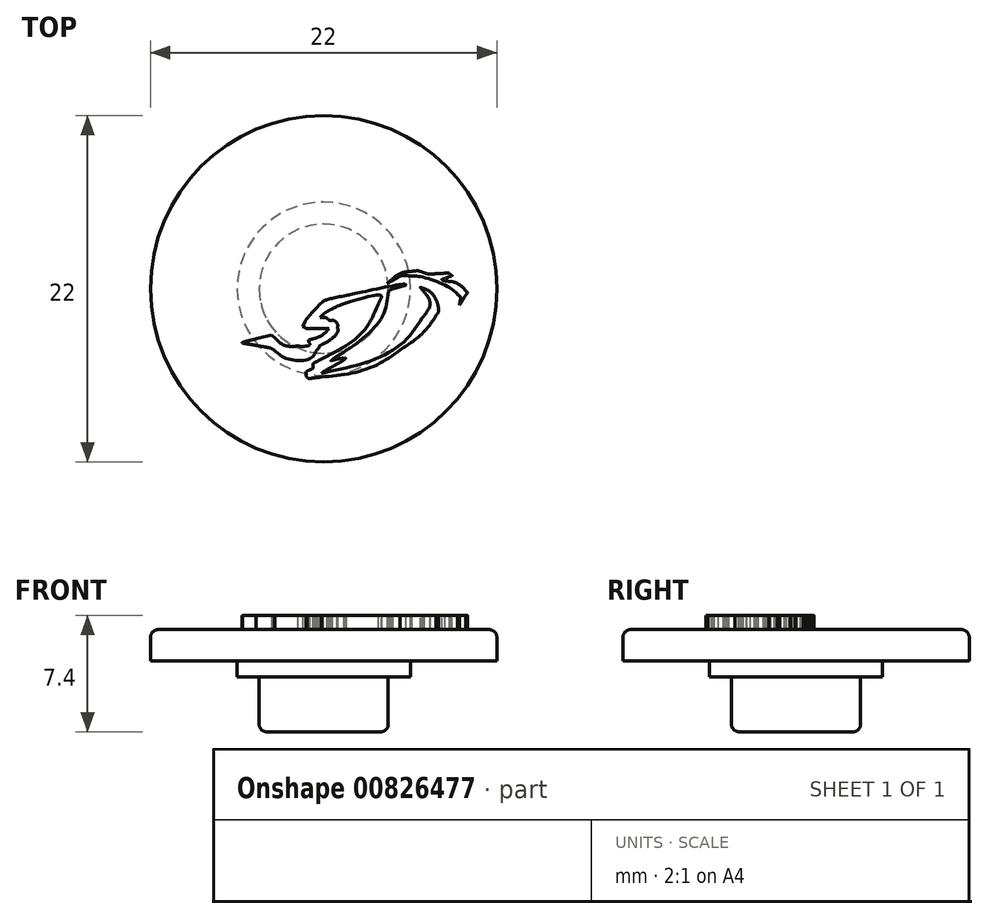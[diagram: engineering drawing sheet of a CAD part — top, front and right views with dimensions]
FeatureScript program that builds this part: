
annotation { "Feature Type Name" : "Feature", "Feature Type Description" : "" }
export const myFeature = defineFeature(function(context is Context, id is Id, definition is map)
    precondition{}
    {
        {
            var Q0;
            Q0=qCreatedBy(makeId("Top.planeOp"),FACE);
            var sketch = newSketch(context, id + "F0", { "sketchPlane" : qUnion([Q0])});
            skFitSpline(sketch, "E0", {"points": [v(-1.06, -5.63) * mm, v(-1.1, -5.6) * mm, v(-1.12, -5.5) * mm, v(-1.12, -5.4) * mm]});
            skFitSpline(sketch, "E1", {"points": [v(-1.12, -5.4) * mm, v(-1.12, -5.29) * mm, v(-1.08, -5.24) * mm, v(-0.9, -5.16) * mm]});
            skFitSpline(sketch, "E2", {"points": [v(-0.9, -5.16) * mm, v(-0.71, -5.08) * mm, v(-0.68, -5.03) * mm, v(-0.68, -4.9) * mm]});
            skFitSpline(sketch, "E3", {"points": [v(-0.68, -4.9) * mm, v(-0.68, -4.78) * mm, v(-0.63, -4.72) * mm, v(-0.5, -4.65) * mm]});
            skFitSpline(sketch, "E4", {"points": [v(-0.5, -4.65) * mm, v(1.5, -3.55) * mm, v(2.75, -2.4) * mm, v(3.43, -1.03) * mm]});
            skFitSpline(sketch, "E5", {"points": [v(3.43, -1.03) * mm, v(3.58, -0.74) * mm, v(3.68, -0.5) * mm, v(3.66, -0.48) * mm]});
            skFitSpline(sketch, "E6", {"points": [v(3.66, -0.48) * mm, v(3.57, -0.4) * mm, v(1.07, -1.04) * mm, v(0.53, -1.29) * mm]});
            skFitSpline(sketch, "E7", {"points": [v(0.53, -1.29) * mm, v(0.34, -1.37) * mm, v(0.09, -1.53) * mm, v(-0.03, -1.64) * mm]});
            skFitSpline(sketch, "E8", {"points": [v(-0.05, -1.83) * mm, v(0.06, -1.83) * mm, v(0.2, -1.87) * mm, v(0.26, -1.92) * mm]});
            skFitSpline(sketch, "E9", {"points": [v(0.26, -1.92) * mm, v(0.32, -1.97) * mm, v(0.42, -2.02) * mm, v(0.49, -2.02) * mm]});
            skFitSpline(sketch, "E10", {"points": [v(0.49, -2.02) * mm, v(0.66, -2.02) * mm, v(0.88, -2.26) * mm, v(0.88, -2.45) * mm]});
            skFitSpline(sketch, "E11", {"points": [v(0.88, -2.45) * mm, v(0.88, -2.74) * mm, v(0.48, -3.2) * mm, v(-0.04, -3.5) * mm]});
            skFitSpline(sketch, "E12", {"points": [v(-0.04, -3.5) * mm, v(-0.18, -3.58) * mm, v(-0.29, -3.66) * mm, v(-0.29, -3.7) * mm]});
            skFitSpline(sketch, "E13", {"points": [v(-0.29, -3.7) * mm, v(-0.29, -3.72) * mm, v(-0.36, -3.83) * mm, v(-0.46, -3.93) * mm]});
            skFitSpline(sketch, "E14", {"points": [v(-0.46, -3.93) * mm, v(-0.91, -4.45) * mm, v(-2.3, -4.45) * mm, v(-3.14, -3.92) * mm]});
            skFitSpline(sketch, "E15", {"points": [v(-3.14, -3.92) * mm, v(-3.35, -3.79) * mm, v(-3.55, -3.73) * mm, v(-4.3, -3.6) * mm]});
            skFitSpline(sketch, "E16", {"points": [v(-4.3, -3.6) * mm, v(-4.79, -3.52) * mm, v(-5.18, -3.44) * mm, v(-5.17, -3.42) * mm]});
            skFitSpline(sketch, "E17", {"points": [v(-5.17, -3.42) * mm, v(-5.16, -3.41) * mm, v(-4.74, -3.3) * mm, v(-4.23, -3.16) * mm]});
            skLineSegment(sketch, "E18", {"start": v(-0.03, -1.64) * mm, "end": v(-0.25, -1.83) * mm});
            skLineSegment(sketch, "E19", {"start": v(-0.25, -1.83) * mm, "end": v(-0.05, -1.83) * mm});
            skFitSpline(sketch, "E20", {"points": [v(-3.06, -3.16) * mm, v(-2.68, -3.5) * mm, v(-2.27, -3.65) * mm, v(-1.67, -3.65) * mm]});
            skFitSpline(sketch, "E21", {"points": [v(-1.67, -3.65) * mm, v(-1.13, -3.65) * mm, v(-0.89, -3.55) * mm, v(-0.94, -3.37) * mm]});
            skFitSpline(sketch, "E22", {"points": [v(-0.94, -3.37) * mm, v(-0.96, -3.28) * mm, v(-0.91, -3.25) * mm, v(-0.72, -3.2) * mm]});
            skFitSpline(sketch, "E23", {"points": [v(-0.72, -3.2) * mm, v(-0.4, -3.1) * mm, v(0.01, -2.87) * mm, v(0.19, -2.68) * mm]});
            skLineSegment(sketch, "E24", {"start": v(-4.23, -3.16) * mm, "end": v(-3.32, -2.92) * mm});
            skLineSegment(sketch, "E25", {"start": v(-3.32, -2.92) * mm, "end": v(-3.06, -3.16) * mm});
            skFitSpline(sketch, "E26", {"points": [v(-0.35, -2.53) * mm, v(-0.78, -2.54) * mm, v(-1.1, -2.52) * mm, v(-1.2, -2.47) * mm]});
            skLineSegment(sketch, "E27", {"start": v(0.19, -2.68) * mm, "end": v(0.34, -2.53) * mm});
            skLineSegment(sketch, "E28", {"start": v(0.34, -2.53) * mm, "end": v(-0.35, -2.53) * mm});
            skFitSpline(sketch, "E29", {"points": [v(-1.2, -2.11) * mm, v(-1.1, -1.95) * mm, v(-0.85, -1.63) * mm, v(-0.62, -1.4) * mm]});
            skFitSpline(sketch, "E30", {"points": [v(-0.62, -1.4) * mm, v(-0.06, -0.83) * mm, v(0.27, -0.67) * mm, v(1.42, -0.43) * mm]});
            skFitSpline(sketch, "E31", {"points": [v(1.42, -0.43) * mm, v(2.5, -0.2) * mm, v(5.18, 0.29) * mm, v(5.21, 0.25) * mm]});
            skFitSpline(sketch, "E32", {"points": [v(5.21, 0.25) * mm, v(5.22, 0.24) * mm, v(5.03, 0.17) * mm, v(4.77, 0.1) * mm]});
            skFitSpline(sketch, "E33", {"points": [v(4.77, 0.1) * mm, v(4.52, 0.03) * mm, v(4.27, -0.05) * mm, v(4.23, -0.07) * mm]});
            skFitSpline(sketch, "E34", {"points": [v(4.23, -0.07) * mm, v(4.18, -0.1) * mm, v(4.1, -0.25) * mm, v(4.07, -0.4) * mm]});
            skFitSpline(sketch, "E35", {"points": [v(4.07, -0.4) * mm, v(3.8, -1.62) * mm, v(2.55, -3.1) * mm, v(0.83, -4.3) * mm]});
            skFitSpline(sketch, "E36", {"points": [v(0.83, -4.3) * mm, v(0.6, -4.46) * mm, v(0.46, -4.58) * mm, v(0.52, -4.56) * mm]});
            skFitSpline(sketch, "E37", {"points": [v(0.52, -4.56) * mm, v(0.8, -4.48) * mm, v(1.15, -4.42) * mm, v(1.27, -4.42) * mm]});
            skFitSpline(sketch, "E38", {"points": [v(1.27, -4.42) * mm, v(1.41, -4.42) * mm, v(1.41, -4.42) * mm, v(1.3, -4.5) * mm]});
            skFitSpline(sketch, "E39", {"points": [v(1.3, -4.5) * mm, v(1.24, -4.55) * mm, v(0.9, -4.75) * mm, v(0.54, -4.96) * mm]});
            skFitSpline(sketch, "E40", {"points": [v(0.54, -4.96) * mm, v(0.18, -5.16) * mm, v(-0.1, -5.33) * mm, v(-0.1, -5.34) * mm]});
            skFitSpline(sketch, "E41", {"points": [v(-0.1, -5.34) * mm, v(-0.09, -5.35) * mm, v(0.17, -5.3) * mm, v(0.47, -5.22) * mm]});
            skFitSpline(sketch, "E42", {"points": [v(0.47, -5.22) * mm, v(3.05, -4.56) * mm, v(5.1, -3.36) * mm, v(6.26, -1.86) * mm]});
            skFitSpline(sketch, "E43", {"points": [v(6.26, -1.86) * mm, v(6.51, -1.53) * mm, v(6.74, -1.12) * mm, v(6.74, -1) * mm]});
            skFitSpline(sketch, "E44", {"points": [v(6.74, -1) * mm, v(6.74, -0.79) * mm, v(6.6, -0.47) * mm, v(6.37, -0.2) * mm]});
            skFitSpline(sketch, "E45", {"points": [v(6.37, -0.2) * mm, v(6.14, 0.08) * mm, v(6.14, 0.1) * mm, v(6.28, 0.04) * mm]});
            skFitSpline(sketch, "E46", {"points": [v(6.28, 0.04) * mm, v(6.55, -0.06) * mm, v(6.95, -0.39) * mm, v(7.1, -0.64) * mm]});
            skFitSpline(sketch, "E47", {"points": [v(7.1, -0.64) * mm, v(7.18, -0.78) * mm, v(7.26, -1.01) * mm, v(7.28, -1.17) * mm]});
            skFitSpline(sketch, "E48", {"points": [v(7.28, -1.17) * mm, v(7.3, -1.42) * mm, v(7.3, -1.47) * mm, v(7.13, -1.7) * mm]});
            skFitSpline(sketch, "E49", {"points": [v(7.13, -1.7) * mm, v(6.62, -2.45) * mm, v(5.76, -3.27) * mm, v(4.84, -3.88) * mm]});
            skFitSpline(sketch, "E50", {"points": [v(4.84, -3.88) * mm, v(3.56, -4.74) * mm, v(1.78, -5.36) * mm, v(-0.14, -5.6) * mm]});
            skFitSpline(sketch, "E51", {"points": [v(-0.14, -5.6) * mm, v(-0.95, -5.71) * mm, v(-0.97, -5.71) * mm, v(-1.06, -5.63) * mm]});
            skLineSegment(sketch, "E52", {"start": v(-1.2, -2.47) * mm, "end": v(-1.35, -2.4) * mm});
            skLineSegment(sketch, "E53", {"start": v(-1.35, -2.4) * mm, "end": v(-1.2, -2.11) * mm});
            skFitSpline(sketch, "E54", {"points": [v(-5.56, -2.37) * mm, v(-5.18, -1.6) * mm, v(-5.14, -0.8) * mm, v(-5.47, -0.19) * mm]});
            skFitSpline(sketch, "E55", {"points": [v(-5.47, -0.19) * mm, v(-6.03, 0.87) * mm, v(-7.3, 1.6) * mm, v(-9.85, 2.35) * mm]});
            skFitSpline(sketch, "E56", {"points": [v(-9.85, 2.35) * mm, v(-10.11, 2.43) * mm, v(-10.08, 2.43) * mm, v(-8.98, 2.44) * mm]});
            skFitSpline(sketch, "E57", {"points": [v(-8.98, 2.44) * mm, v(-8.05, 2.44) * mm, v(-7.74, 2.46) * mm, v(-7.29, 2.55) * mm]});
            skFitSpline(sketch, "E58", {"points": [v(-7.29, 2.55) * mm, v(-6.56, 2.7) * mm, v(-6.58, 2.7) * mm, v(-6.7, 2.46) * mm]});
            skFitSpline(sketch, "E59", {"points": [v(-6.7, 2.46) * mm, v(-6.9, 2.05) * mm, v(-6.9, 2.03) * mm, v(-6.56, 1.87) * mm]});
            skLineSegment(sketch, "E60", {"start": v(-1.06, -5.63) * mm, "end": v(-1.06, -5.63) * mm});
            skFitSpline(sketch, "E61", {"points": [v(-6.01, 2.05) * mm, v(-5.8, 2.33) * mm, v(-5.16, 2.83) * mm, v(-5.02, 2.83) * mm]});
            skFitSpline(sketch, "E62", {"points": [v(-5.02, 2.83) * mm, v(-4.93, 2.83) * mm, v(-4.97, 2.71) * mm, v(-5.14, 2.5) * mm]});
            skFitSpline(sketch, "E63", {"points": [v(-5.14, 2.5) * mm, v(-5.3, 2.3) * mm, v(-5.6, 1.7) * mm, v(-5.66, 1.47) * mm]});
            skFitSpline(sketch, "E64", {"points": [v(-5.66, 1.47) * mm, v(-5.68, 1.38) * mm, v(-5.62, 1.3) * mm, v(-5.4, 1.13) * mm]});
            skLineSegment(sketch, "E65", {"start": v(-6.56, 1.87) * mm, "end": v(-6.26, 1.73) * mm});
            skLineSegment(sketch, "E66", {"start": v(-6.26, 1.73) * mm, "end": v(-6.01, 2.05) * mm});
            skFitSpline(sketch, "E67", {"points": [v(-4.98, 1.2) * mm, v(-4.9, 1.36) * mm, v(-4.76, 1.6) * mm, v(-4.65, 1.75) * mm]});
            skFitSpline(sketch, "E68", {"points": [v(-4.65, 1.75) * mm, v(-4.46, 2) * mm, v(-3.84, 2.5) * mm, v(-3.74, 2.5) * mm]});
            skFitSpline(sketch, "E69", {"points": [v(-3.74, 2.5) * mm, v(-3.63, 2.5) * mm, v(-3.7, 2.32) * mm, v(-3.93, 1.98) * mm]});
            skFitSpline(sketch, "E70", {"points": [v(-3.93, 1.98) * mm, v(-4.28, 1.47) * mm, v(-4.4, 1) * mm, v(-4.47, 0.07) * mm]});
            skFitSpline(sketch, "E71", {"points": [v(-4.47, 0.07) * mm, v(-4.52, -0.75) * mm, v(-4.61, -1.2) * mm, v(-4.8, -1.59) * mm]});
            skFitSpline(sketch, "E72", {"points": [v(-4.8, -1.59) * mm, v(-4.98, -1.92) * mm, v(-5.33, -2.38) * mm, v(-5.53, -2.52) * mm]});
            skLineSegment(sketch, "E73", {"start": v(-5.4, 1.13) * mm, "end": v(-5.1, 0.9) * mm});
            skLineSegment(sketch, "E74", {"start": v(-5.1, 0.9) * mm, "end": v(-4.98, 1.2) * mm});
            skFitSpline(sketch, "E75", {"points": [v(-3.23, -2.03) * mm, v(-3.24, -1.56) * mm, v(-3.08, -1.14) * mm, v(-2.74, -0.77) * mm]});
            skFitSpline(sketch, "E76", {"points": [v(-2.74, -0.77) * mm, v(-2.59, -0.6) * mm, v(-2.35, -0.41) * mm, v(-2.21, -0.34) * mm]});
            skFitSpline(sketch, "E77", {"points": [v(-2.21, -0.34) * mm, v(-2, -0.22) * mm, v(-1.94, -0.17) * mm, v(-1.87, 0.07) * mm]});
            skFitSpline(sketch, "E78", {"points": [v(-1.87, 0.07) * mm, v(-1.78, 0.38) * mm, v(-1.77, 0.65) * mm, v(-1.84, 0.77) * mm]});
            skFitSpline(sketch, "E79", {"points": [v(-1.84, 0.77) * mm, v(-1.92, 0.88) * mm, v(-2.24, 0.82) * mm, v(-2.8, 0.58) * mm]});
            skFitSpline(sketch, "E80", {"points": [v(-2.8, 0.58) * mm, v(-3.7, 0.2) * mm, v(-3.91, -0.03) * mm, v(-3.9, -0.59) * mm]});
            skFitSpline(sketch, "E81", {"points": [v(-3.9, -0.59) * mm, v(-3.9, -0.78) * mm, v(-3.89, -1.02) * mm, v(-3.86, -1.14) * mm]});
            skFitSpline(sketch, "E82", {"points": [v(-3.86, -1.14) * mm, v(-3.83, -1.25) * mm, v(-3.83, -1.33) * mm, v(-3.85, -1.32) * mm]});
            skFitSpline(sketch, "E83", {"points": [v(-3.85, -1.32) * mm, v(-3.95, -1.26) * mm, v(-4.03, -0.54) * mm, v(-4, -0.07) * mm]});
            skFitSpline(sketch, "E84", {"points": [v(-4, -0.07) * mm, v(-3.97, 0.46) * mm, v(-3.83, 0.92) * mm, v(-3.55, 1.34) * mm]});
            skLineSegment(sketch, "E85", {"start": v(-5.53, -2.52) * mm, "end": v(-5.7, -2.64) * mm});
            skLineSegment(sketch, "E86", {"start": v(-5.7, -2.64) * mm, "end": v(-5.56, -2.37) * mm});
            skFitSpline(sketch, "E87", {"points": [v(-1.57, 1.6) * mm, v(0.18, 1.6) * mm, v(0.24, 1.61) * mm, v(0.43, 1.73) * mm]});
            skFitSpline(sketch, "E88", {"points": [v(0.43, 1.73) * mm, v(1.18, 2.18) * mm, v(1.72, 2.78) * mm, v(1.83, 3.3) * mm]});
            skFitSpline(sketch, "E89", {"points": [v(1.83, 3.3) * mm, v(1.9, 3.58) * mm, v(1.85, 3.94) * mm, v(1.7, 4.29) * mm]});
            skFitSpline(sketch, "E90", {"points": [v(1.7, 4.29) * mm, v(1.66, 4.37) * mm, v(1.74, 4.38) * mm, v(2.23, 4.42) * mm]});
            skFitSpline(sketch, "E91", {"points": [v(2.23, 4.42) * mm, v(2.55, 4.44) * mm, v(2.93, 4.47) * mm, v(3.09, 4.48) * mm]});
            skLineSegment(sketch, "E92", {"start": v(-3.55, 1.34) * mm, "end": v(-3.38, 1.6) * mm});
            skLineSegment(sketch, "E93", {"start": v(-3.38, 1.6) * mm, "end": v(-1.57, 1.6) * mm});
            skFitSpline(sketch, "E94", {"points": [v(3.2, 4.42) * mm, v(2.95, 4.28) * mm, v(2.62, 3.95) * mm, v(2.48, 3.7) * mm]});
            skFitSpline(sketch, "E95", {"points": [v(2.48, 3.7) * mm, v(2.38, 3.52) * mm, v(2.36, 3.38) * mm, v(2.36, 2.97) * mm]});
            skFitSpline(sketch, "E96", {"points": [v(2.36, 2.97) * mm, v(2.36, 2.45) * mm, v(2.41, 2.3) * mm, v(2.7, 1.9) * mm]});
            skLineSegment(sketch, "E97", {"start": v(3.09, 4.48) * mm, "end": v(3.36, 4.51) * mm});
            skLineSegment(sketch, "E98", {"start": v(3.36, 4.51) * mm, "end": v(3.2, 4.42) * mm});
            skFitSpline(sketch, "E99", {"points": [v(6.72, 1.57) * mm, v(7.03, 1.42) * mm, v(7.45, 1.37) * mm, v(7.76, 1.46) * mm]});
            skLineSegment(sketch, "E100", {"start": v(2.7, 1.9) * mm, "end": v(2.84, 1.72) * mm});
            skLineSegment(sketch, "E101", {"start": v(2.84, 1.72) * mm, "end": v(4.63, 1.72) * mm});
            skLineSegment(sketch, "E102", {"start": v(4.63, 1.72) * mm, "end": v(6.42, 1.72) * mm});
            skLineSegment(sketch, "E103", {"start": v(6.42, 1.72) * mm, "end": v(6.72, 1.57) * mm});
            skFitSpline(sketch, "E104", {"points": [v(7.53, 1.91) * mm, v(7.15, 2.31) * mm, v(6.96, 2.62) * mm, v(6.96, 2.8) * mm]});
            skFitSpline(sketch, "E105", {"points": [v(6.96, 2.8) * mm, v(6.96, 2.97) * mm, v(6.67, 3.54) * mm, v(6.44, 3.8) * mm]});
            skLineSegment(sketch, "E106", {"start": v(7.76, 1.46) * mm, "end": v(7.92, 1.5) * mm});
            skLineSegment(sketch, "E107", {"start": v(7.92, 1.5) * mm, "end": v(7.53, 1.91) * mm});
            skFitSpline(sketch, "E108", {"points": [v(6.54, 3.9) * mm, v(7.28, 3.49) * mm, v(7.31, 3.45) * mm, v(7.4, 3.06) * mm]});
            skFitSpline(sketch, "E109", {"points": [v(7.4, 3.06) * mm, v(7.47, 2.66) * mm, v(7.5, 2.6) * mm, v(7.85, 2.21) * mm]});
            skFitSpline(sketch, "E110", {"points": [v(7.85, 2.21) * mm, v(8.02, 2.02) * mm, v(8.24, 1.86) * mm, v(8.73, 1.62) * mm]});
            skLineSegment(sketch, "E111", {"start": v(6.44, 3.8) * mm, "end": v(6.2, 4.09) * mm});
            skLineSegment(sketch, "E112", {"start": v(6.2, 4.09) * mm, "end": v(6.54, 3.9) * mm});
            skFitSpline(sketch, "E113", {"points": [v(9.7, -0.6) * mm, v(9.54, -0.8) * mm, v(9.36, -1.06) * mm, v(9.3, -1.18) * mm]});
            skFitSpline(sketch, "E114", {"points": [v(9.3, -1.18) * mm, v(9.17, -1.44) * mm, v(9.13, -1.47) * mm, v(8.63, -1.65) * mm]});
            skLineSegment(sketch, "E115", {"start": v(8.73, 1.62) * mm, "end": v(9.38, 1.28) * mm});
            skLineSegment(sketch, "E116", {"start": v(9.38, 1.28) * mm, "end": v(9.69, 0.53) * mm});
            skLineSegment(sketch, "E117", {"start": v(9.69, 0.53) * mm, "end": v(9.99, -0.22) * mm});
            skLineSegment(sketch, "E118", {"start": v(9.99, -0.22) * mm, "end": v(9.7, -0.6) * mm});
            skFitSpline(sketch, "E119", {"points": [v(8.61, -1.4) * mm, v(8.85, -1.14) * mm, v(9.09, -0.83) * mm, v(9.2, -0.6) * mm]});
            skLineSegment(sketch, "E120", {"start": v(8.63, -1.65) * mm, "end": v(8.21, -1.8) * mm});
            skLineSegment(sketch, "E121", {"start": v(8.21, -1.8) * mm, "end": v(8.61, -1.4) * mm});
            skFitSpline(sketch, "E122", {"points": [v(9.19, 0.08) * mm, v(9.07, 0.24) * mm, v(8.88, 0.45) * mm, v(8.77, 0.53) * mm]});
            skFitSpline(sketch, "E123", {"points": [v(8.77, 0.53) * mm, v(8.55, 0.71) * mm, v(8.53, 0.77) * mm, v(8.7, 0.77) * mm]});
            skFitSpline(sketch, "E124", {"points": [v(8.7, 0.77) * mm, v(8.84, 0.77) * mm, v(9.02, 0.87) * mm, v(9.02, 0.94) * mm]});
            skFitSpline(sketch, "E125", {"points": [v(9.02, 0.94) * mm, v(9.02, 0.98) * mm, v(8.81, 1.1) * mm, v(8.55, 1.22) * mm]});
            skLineSegment(sketch, "E126", {"start": v(9.2, -0.6) * mm, "end": v(9.41, -0.21) * mm});
            skLineSegment(sketch, "E127", {"start": v(9.41, -0.21) * mm, "end": v(9.19, 0.08) * mm});
            skFitSpline(sketch, "E128", {"points": [v(7.82, 1.32) * mm, v(7.45, 1.16) * mm, v(6.85, 1.12) * mm, v(6.4, 1.25) * mm]});
            skFitSpline(sketch, "E129", {"points": [v(6.4, 1.25) * mm, v(5.72, 1.43) * mm, v(4.97, 1.3) * mm, v(4.35, 0.9) * mm]});
            skLineSegment(sketch, "E130", {"start": v(8.55, 1.22) * mm, "end": v(8.08, 1.44) * mm});
            skLineSegment(sketch, "E131", {"start": v(8.08, 1.44) * mm, "end": v(7.82, 1.32) * mm});
            skFitSpline(sketch, "E132", {"points": [v(4.06, 0.91) * mm, v(4.06, 1.17) * mm, v(3.94, 1.21) * mm, v(3.3, 1.22) * mm]});
            skFitSpline(sketch, "E133", {"points": [v(3.3, 1.22) * mm, v(2.7, 1.23) * mm, v(2.58, 1.18) * mm, v(2.2, 0.82) * mm]});
            skLineSegment(sketch, "E134", {"start": v(4.35, 0.9) * mm, "end": v(4.06, 0.71) * mm});
            skLineSegment(sketch, "E135", {"start": v(4.06, 0.71) * mm, "end": v(4.06, 0.91) * mm});
            skFitSpline(sketch, "E136", {"points": [v(1.64, 0.6) * mm, v(1.4, 0.67) * mm, v(1.39, 0.68) * mm, v(1.39, 0.88) * mm]});
            skFitSpline(sketch, "E137", {"points": [v(1.39, 0.88) * mm, v(1.39, 0.99) * mm, v(1.41, 1.17) * mm, v(1.44, 1.27) * mm]});
            skLineSegment(sketch, "E138", {"start": v(2.2, 0.82) * mm, "end": v(1.9, 0.54) * mm});
            skLineSegment(sketch, "E139", {"start": v(1.9, 0.54) * mm, "end": v(1.64, 0.6) * mm});
            skFitSpline(sketch, "E140", {"points": [v(1.36, 1.31) * mm, v(1.28, 1.23) * mm, v(1.18, 1.04) * mm, v(1.13, 0.89) * mm]});
            skFitSpline(sketch, "E141", {"points": [v(1.13, 0.89) * mm, v(1.04, 0.64) * mm, v(1.01, 0.61) * mm, v(0.83, 0.59) * mm]});
            skFitSpline(sketch, "E142", {"points": [v(0.83, 0.59) * mm, v(0.72, 0.58) * mm, v(0.62, 0.58) * mm, v(0.6, 0.59) * mm]});
            skFitSpline(sketch, "E143", {"points": [v(0.6, 0.59) * mm, v(0.6, 0.6) * mm, v(0.56, 0.75) * mm, v(0.55, 0.93) * mm]});
            skLineSegment(sketch, "E144", {"start": v(1.44, 1.27) * mm, "end": v(1.5, 1.47) * mm});
            skLineSegment(sketch, "E145", {"start": v(1.5, 1.47) * mm, "end": v(1.36, 1.31) * mm});
            skFitSpline(sketch, "E146", {"points": [v(0.42, 1.03) * mm, v(0.37, 0.91) * mm, v(0.33, 0.74) * mm, v(0.33, 0.66) * mm]});
            skFitSpline(sketch, "E147", {"points": [v(0.33, 0.66) * mm, v(0.33, 0.56) * mm, v(0.28, 0.47) * mm, v(0.18, 0.41) * mm]});
            skFitSpline(sketch, "E148", {"points": [v(0.18, 0.41) * mm, v(0.01, 0.3) * mm, v(0.02, 0.3) * mm, v(-0.15, 0.64) * mm]});
            skLineSegment(sketch, "E149", {"start": v(0.55, 0.93) * mm, "end": v(0.52, 1.24) * mm});
            skLineSegment(sketch, "E150", {"start": v(0.52, 1.24) * mm, "end": v(0.42, 1.03) * mm});
            skFitSpline(sketch, "E151", {"points": [v(-0.28, 0.55) * mm, v(-0.26, 0.19) * mm, v(-0.35, -0.07) * mm, v(-0.49, -0.07) * mm]});
            skFitSpline(sketch, "E152", {"points": [v(-0.49, -0.07) * mm, v(-0.52, -0.07) * mm, v(-0.64, 0.02) * mm, v(-0.75, 0.13) * mm]});
            skLineSegment(sketch, "E153", {"start": v(-0.15, 0.64) * mm, "end": v(-0.29, 0.91) * mm});
            skLineSegment(sketch, "E154", {"start": v(-0.29, 0.91) * mm, "end": v(-0.28, 0.55) * mm});
            skFitSpline(sketch, "E155", {"points": [v(-0.92, 0.18) * mm, v(-0.9, 0.09) * mm, v(-0.85, -0.05) * mm, v(-0.81, -0.14) * mm]});
            skFitSpline(sketch, "E156", {"points": [v(-0.81, -0.14) * mm, v(-0.77, -0.23) * mm, v(-0.75, -0.36) * mm, v(-0.77, -0.43) * mm]});
            skFitSpline(sketch, "E157", {"points": [v(-0.77, -0.43) * mm, v(-0.8, -0.54) * mm, v(-0.83, -0.56) * mm, v(-1.3, -0.58) * mm]});
            skFitSpline(sketch, "E158", {"points": [v(-1.3, -0.58) * mm, v(-1.72, -0.6) * mm, v(-1.87, -0.63) * mm, v(-2.1, -0.75) * mm]});
            skFitSpline(sketch, "E159", {"points": [v(-2.1, -0.75) * mm, v(-2.62, -1.02) * mm, v(-3.08, -1.6) * mm, v(-3.18, -2.15) * mm]});
            skFitSpline(sketch, "E160", {"points": [v(-3.18, -2.15) * mm, v(-3.23, -2.37) * mm, v(-3.23, -2.37) * mm, v(-3.23, -2.03) * mm]});
            skLineSegment(sketch, "E161", {"start": v(-0.75, 0.13) * mm, "end": v(-0.96, 0.33) * mm});
            skLineSegment(sketch, "E162", {"start": v(-0.96, 0.33) * mm, "end": v(-0.92, 0.18) * mm});
            skFitSpline(sketch, "E163", {"points": [v(8.67, -0.79) * mm, v(8.7, -0.54) * mm, v(8.7, -0.52) * mm, v(8.49, -0.35) * mm]});
            skFitSpline(sketch, "E164", {"points": [v(8.49, -0.35) * mm, v(7.97, 0.08) * mm, v(6.23, 0.75) * mm, v(5.49, 0.81) * mm]});
            skFitSpline(sketch, "E165", {"points": [v(5.49, 0.81) * mm, v(5.02, 0.85) * mm, v(4.83, 0.8) * mm, v(4.36, 0.52) * mm]});
            skFitSpline(sketch, "E166", {"points": [v(4.26, 0.52) * mm, v(4.6, 0.83) * mm, v(5.1, 1.04) * mm, v(5.57, 1.1) * mm]});
            skFitSpline(sketch, "E167", {"points": [v(5.57, 1.1) * mm, v(5.93, 1.15) * mm, v(6.03, 1.14) * mm, v(6.32, 1.04) * mm]});
            skFitSpline(sketch, "E168", {"points": [v(6.32, 1.04) * mm, v(6.61, 0.94) * mm, v(6.73, 0.93) * mm, v(7.3, 0.96) * mm]});
            skFitSpline(sketch, "E169", {"points": [v(7.3, 0.96) * mm, v(7.82, 1) * mm, v(7.96, 0.99) * mm, v(8.05, 0.92) * mm]});
            skFitSpline(sketch, "E170", {"points": [v(8.05, 0.92) * mm, v(8.16, 0.84) * mm, v(8.15, 0.83) * mm, v(8, 0.77) * mm]});
            skFitSpline(sketch, "E171", {"points": [v(8, 0.77) * mm, v(7.9, 0.73) * mm, v(7.76, 0.68) * mm, v(7.68, 0.65) * mm]});
            skFitSpline(sketch, "E172", {"points": [v(7.68, 0.65) * mm, v(7.51, 0.58) * mm, v(7.6, 0.52) * mm, v(7.95, 0.47) * mm]});
            skFitSpline(sketch, "E173", {"points": [v(7.95, 0.47) * mm, v(8.28, 0.42) * mm, v(8.73, 0.19) * mm, v(8.96, -0.05) * mm]});
            skFitSpline(sketch, "E174", {"points": [v(8.96, -0.05) * mm, v(9.13, -0.23) * mm, v(9.13, -0.25) * mm, v(9.05, -0.36) * mm]});
            skFitSpline(sketch, "E175", {"points": [v(9.05, -0.36) * mm, v(9, -0.43) * mm, v(8.9, -0.6) * mm, v(8.8, -0.76) * mm]});
            skLineSegment(sketch, "E176", {"start": v(4.36, 0.52) * mm, "end": v(4.03, 0.32) * mm});
            skLineSegment(sketch, "E177", {"start": v(4.03, 0.32) * mm, "end": v(4.26, 0.52) * mm});
            skFitSpline(sketch, "E178", {"points": [v(-1.07, 2.14) * mm, v(-1.07, 2.15) * mm, v(-1.03, 2.26) * mm, v(-0.99, 2.36) * mm]});
            skLineSegment(sketch, "E179", {"start": v(8.8, -0.76) * mm, "end": v(8.63, -1.04) * mm});
            skLineSegment(sketch, "E180", {"start": v(8.63, -1.04) * mm, "end": v(8.67, -0.79) * mm});
            skFitSpline(sketch, "E181", {"points": [v(-1.18, 2.67) * mm, v(-1.42, 2.78) * mm, v(-1.84, 3.14) * mm, v(-1.78, 3.2) * mm]});
            skFitSpline(sketch, "E182", {"points": [v(-1.78, 3.2) * mm, v(-1.77, 3.2) * mm, v(-1.62, 3.15) * mm, v(-1.45, 3.07) * mm]});
            skFitSpline(sketch, "E183", {"points": [v(-1.45, 3.07) * mm, v(-1.25, 2.97) * mm, v(-1.03, 2.92) * mm, v(-0.76, 2.9) * mm]});
            skLineSegment(sketch, "E184", {"start": v(-0.99, 2.36) * mm, "end": v(-0.9, 2.55) * mm});
            skLineSegment(sketch, "E185", {"start": v(-0.9, 2.55) * mm, "end": v(-1.18, 2.67) * mm});
            skFitSpline(sketch, "E186", {"points": [v(0.01, 3.3) * mm, v(0.37, 3.7) * mm, v(0.4, 3.72) * mm, v(0.68, 3.76) * mm]});
            skFitSpline(sketch, "E187", {"points": [v(0.68, 3.76) * mm, v(1.18, 3.83) * mm, v(1.21, 3.86) * mm, v(0.9, 4) * mm]});
            skFitSpline(sketch, "E188", {"points": [v(0.9, 4) * mm, v(0.34, 4.23) * mm, v(0.34, 4.23) * mm, v(-0.06, 3.73) * mm]});
            skFitSpline(sketch, "E189", {"points": [v(-0.06, 3.73) * mm, v(-0.26, 3.48) * mm, v(-0.43, 3.29) * mm, v(-0.43, 3.3) * mm]});
            skFitSpline(sketch, "E190", {"points": [v(-0.43, 3.3) * mm, v(-0.44, 3.3) * mm, v(-0.38, 3.53) * mm, v(-0.29, 3.8) * mm]});
            skFitSpline(sketch, "E191", {"points": [v(-0.29, 3.8) * mm, v(-0.2, 4.07) * mm, v(-0.15, 4.3) * mm, v(-0.18, 4.31) * mm]});
            skFitSpline(sketch, "E192", {"points": [v(-0.18, 4.31) * mm, v(-0.22, 4.34) * mm, v(-0.84, 3.73) * mm, v(-0.9, 3.6) * mm]});
            skFitSpline(sketch, "E193", {"points": [v(-0.9, 3.6) * mm, v(-0.9, 3.58) * mm, v(-0.93, 3.56) * mm, v(-0.96, 3.56) * mm]});
            skFitSpline(sketch, "E194", {"points": [v(-0.96, 3.56) * mm, v(-0.98, 3.56) * mm, v(-0.93, 3.72) * mm, v(-0.84, 3.93) * mm]});
            skFitSpline(sketch, "E195", {"points": [v(-0.84, 3.93) * mm, v(-0.64, 4.37) * mm, v(-0.64, 4.4) * mm, v(-0.81, 4.4) * mm]});
            skFitSpline(sketch, "E196", {"points": [v(-0.81, 4.4) * mm, v(-0.9, 4.4) * mm, v(-1.02, 4.3) * mm, v(-1.18, 4.12) * mm]});
            skFitSpline(sketch, "E197", {"points": [v(-1.18, 4.12) * mm, v(-1.31, 3.96) * mm, v(-1.43, 3.85) * mm, v(-1.44, 3.86) * mm]});
            skFitSpline(sketch, "E198", {"points": [v(-1.44, 3.86) * mm, v(-1.45, 3.87) * mm, v(-1.44, 4) * mm, v(-1.41, 4.17) * mm]});
            skLineSegment(sketch, "E199", {"start": v(-0.76, 2.9) * mm, "end": v(-0.36, 2.88) * mm});
            skLineSegment(sketch, "E200", {"start": v(-0.36, 2.88) * mm, "end": v(0.01, 3.3) * mm});
            skFitSpline(sketch, "E201", {"points": [v(-1.83, 4.45) * mm, v(-2.24, 4.45) * mm, v(-2.3, 4.44) * mm, v(-2.24, 4.37) * mm]});
            skFitSpline(sketch, "E202", {"points": [v(-2.24, 4.37) * mm, v(-2.2, 4.31) * mm, v(-2.2, 4.23) * mm, v(-2.23, 4.07) * mm]});
            skFitSpline(sketch, "E203", {"points": [v(-2.23, 4.07) * mm, v(-2.29, 3.87) * mm, v(-2.31, 3.85) * mm, v(-2.51, 3.82) * mm]});
            skFitSpline(sketch, "E204", {"points": [v(-2.51, 3.82) * mm, v(-2.7, 3.79) * mm, v(-2.86, 3.83) * mm, v(-3.36, 4.01) * mm]});
            skFitSpline(sketch, "E205", {"points": [v(-3.36, 4.01) * mm, v(-4.04, 4.27) * mm, v(-4.04, 4.28) * mm, v(-3.45, 4.4) * mm]});
            skFitSpline(sketch, "E206", {"points": [v(-3.45, 4.4) * mm, v(-3.17, 4.45) * mm, v(-3.13, 4.47) * mm, v(-3.13, 4.59) * mm]});
            skFitSpline(sketch, "E207", {"points": [v(-3.13, 4.59) * mm, v(-3.13, 4.66) * mm, v(-3.1, 4.74) * mm, v(-3.05, 4.78) * mm]});
            skFitSpline(sketch, "E208", {"points": [v(-3.05, 4.78) * mm, v(-2.95, 4.87) * mm, v(-1.74, 4.96) * mm, v(-1.32, 4.92) * mm]});
            skFitSpline(sketch, "E209", {"points": [v(-1.32, 4.92) * mm, v(-1.03, 4.9) * mm, v(-0.66, 4.95) * mm, v(1.03, 5.29) * mm]});
            skLineSegment(sketch, "E210", {"start": v(-1.41, 4.17) * mm, "end": v(-1.36, 4.45) * mm});
            skLineSegment(sketch, "E211", {"start": v(-1.36, 4.45) * mm, "end": v(-1.83, 4.45) * mm});
            skFitSpline(sketch, "E212", {"points": [v(3.76, 5.37) * mm, v(4.16, 5.2) * mm, v(4.5, 5.04) * mm, v(4.52, 5.02) * mm]});
            skFitSpline(sketch, "E213", {"points": [v(4.52, 5.02) * mm, v(4.54, 5) * mm, v(4.2, 5) * mm, v(3.77, 5.02) * mm]});
            skFitSpline(sketch, "E214", {"points": [v(3.77, 5.02) * mm, v(3.06, 5.05) * mm, v(2.9, 5.04) * mm, v(2.36, 4.92) * mm]});
            skFitSpline(sketch, "E215", {"points": [v(2.36, 4.92) * mm, v(1.07, 4.65) * mm, v(0.38, 4.48) * mm, v(0.42, 4.45) * mm]});
            skFitSpline(sketch, "E216", {"points": [v(0.42, 4.45) * mm, v(0.45, 4.43) * mm, v(0.64, 4.35) * mm, v(0.86, 4.26) * mm]});
            skFitSpline(sketch, "E217", {"points": [v(0.86, 4.26) * mm, v(1.07, 4.18) * mm, v(1.3, 4.08) * mm, v(1.35, 4.03) * mm]});
            skFitSpline(sketch, "E218", {"points": [v(1.35, 4.03) * mm, v(1.5, 3.91) * mm, v(1.54, 3.43) * mm, v(1.4, 3.17) * mm]});
            skFitSpline(sketch, "E219", {"points": [v(1.4, 3.17) * mm, v(1.31, 3) * mm, v(1.27, 2.97) * mm, v(1, 2.93) * mm]});
            skFitSpline(sketch, "E220", {"points": [v(1, 2.93) * mm, v(0.58, 2.87) * mm, v(0.07, 2.62) * mm, v(-0.22, 2.34) * mm]});
            skFitSpline(sketch, "E221", {"points": [v(-0.22, 2.34) * mm, v(-0.44, 2.13) * mm, v(-0.48, 2.1) * mm, v(-0.76, 2.1) * mm]});
            skFitSpline(sketch, "E222", {"points": [v(-0.76, 2.1) * mm, v(-0.93, 2.1) * mm, v(-1.07, 2.12) * mm, v(-1.07, 2.14) * mm]});
            skLineSegment(sketch, "E223", {"start": v(1.03, 5.29) * mm, "end": v(3.04, 5.69) * mm});
            skLineSegment(sketch, "E224", {"start": v(3.04, 5.69) * mm, "end": v(3.76, 5.37) * mm});
            skFitSpline(sketch, "E225", {"points": [v(5.68, 2.27) * mm, v(5.68, 2.36) * mm, v(5.64, 2.37) * mm, v(5.41, 2.35) * mm]});
            skFitSpline(sketch, "E226", {"points": [v(5.41, 2.35) * mm, v(5.18, 2.32) * mm, v(5.12, 2.34) * mm, v(4.97, 2.47) * mm]});
            skFitSpline(sketch, "E227", {"points": [v(4.97, 2.47) * mm, v(4.86, 2.56) * mm, v(4.76, 2.7) * mm, v(4.73, 2.85) * mm]});
            skFitSpline(sketch, "E228", {"points": [v(4.73, 2.85) * mm, v(4.68, 3.03) * mm, v(4.55, 3.2) * mm, v(4.21, 3.55) * mm]});
            skFitSpline(sketch, "E229", {"points": [v(4.21, 3.55) * mm, v(3.7, 4.08) * mm, v(3.66, 4.07) * mm, v(4.7, 3.75) * mm]});
            skFitSpline(sketch, "E230", {"points": [v(4.7, 3.75) * mm, v(5.66, 3.46) * mm, v(6.01, 3.17) * mm, v(6.01, 2.7) * mm]});
            skFitSpline(sketch, "E231", {"points": [v(6.01, 2.7) * mm, v(6.01, 2.43) * mm, v(6.38, 2.36) * mm, v(6.6, 2.6) * mm]});
            skFitSpline(sketch, "E232", {"points": [v(6.6, 2.6) * mm, v(6.76, 2.76) * mm, v(6.77, 2.73) * mm, v(6.65, 2.5) * mm]});
            skFitSpline(sketch, "E233", {"points": [v(6.65, 2.5) * mm, v(6.54, 2.28) * mm, v(6.3, 2.16) * mm, v(5.96, 2.16) * mm]});
            skFitSpline(sketch, "E234", {"points": [v(5.96, 2.16) * mm, v(5.72, 2.16) * mm, v(5.68, 2.18) * mm, v(5.68, 2.27) * mm]});
            skLineSegment(sketch, "E235", {"start": v(-1.07, 2.14) * mm, "end": v(-1.07, 2.14) * mm});
            skCircle(sketch, "E236", {"center": v(0, 0) * mm, "radius": 11 * mm});
            skSolve(sketch);
        }
        {
            var Q0;
            Q0=makeQuery(id+"F0.imprint","IMPRINT",FACE,{"disambiguationData":[TD([[makeQuery(id+"F0.imprint","IMPRINT",EDGE,{"derivedFrom":sQuery(id+"F0.wireOp",EDGE,"E0")}),1.0]])]});
            var Q1;
            Q1=makeQuery(id+"F0.imprint","IMPRINT",FACE,{"disambiguationData":[TD([[makeQuery(id+"F0.imprint","IMPRINT",EDGE,{"derivedFrom":sQuery(id+"F0.wireOp",EDGE,"E54")}),-1.0]])]});
            var Q2;
            Q2=makeQuery(id+"F0.imprint","IMPRINT",FACE,{"disambiguationData":[TD([[makeQuery(id+"F0.imprint","IMPRINT",EDGE,{"derivedFrom":sQuery(id+"F0.wireOp",EDGE,"E75")}),-1.0]])]});
            var Q3;
            Q3=makeQuery(id+"F0.imprint","IMPRINT",FACE,{"disambiguationData":[TD([[makeQuery(id+"F0.imprint","IMPRINT",EDGE,{"derivedFrom":sQuery(id+"F0.wireOp",EDGE,"E178")}),-1.0]])]});
            var Q4;
            Q4=makeQuery(id+"F0.imprint","IMPRINT",FACE,{"disambiguationData":[TD([[makeQuery(id+"F0.imprint","IMPRINT",EDGE,{"derivedFrom":sQuery(id+"F0.wireOp",EDGE,"E225")}),-1.0]])]});
            var Q5;
            Q5=makeQuery(id+"F0.imprint","IMPRINT",FACE,{"disambiguationData":[TD([[makeQuery(id+"F0.imprint","IMPRINT",EDGE,{"derivedFrom":sQuery(id+"F0.wireOp",EDGE,"E0")}),-1.0]])]});
            var Q6;
            Q6=makeQuery(id+"F0.imprint","IMPRINT",FACE,{"disambiguationData":[TD([[makeQuery(id+"F0.imprint","IMPRINT",EDGE,{"derivedFrom":sQuery(id+"F0.wireOp",EDGE,"E163")}),-1.0]])]});
            extrude(context, id + "F1", {"entities" : qUnion([Q0, Q1, Q2, Q3, Q4, Q5, Q6]), "oppositeDirection" : true, "depth" : 2 * mm, "offsetDistance" : 25 * mm});
        }
        {
            var Q0;
            Q0=makeQuery(id+"F0.imprint","IMPRINT",FACE,{"disambiguationData":[TD([[makeQuery(id+"F0.imprint","IMPRINT",EDGE,{"derivedFrom":sQuery(id+"F0.wireOp",EDGE,"E54")}),-1.0]])]});
            var Q1;
            Q1=makeQuery(id+"F0.imprint","IMPRINT",FACE,{"disambiguationData":[TD([[makeQuery(id+"F0.imprint","IMPRINT",EDGE,{"derivedFrom":sQuery(id+"F0.wireOp",EDGE,"E75")}),-1.0]])]});
            var Q2;
            Q2=makeQuery(id+"F0.imprint","IMPRINT",FACE,{"disambiguationData":[TD([[makeQuery(id+"F0.imprint","IMPRINT",EDGE,{"derivedFrom":sQuery(id+"F0.wireOp",EDGE,"E178")}),-1.0]])]});
            var Q3;
            Q3=makeQuery(id+"F0.imprint","IMPRINT",FACE,{"disambiguationData":[TD([[makeQuery(id+"F0.imprint","IMPRINT",EDGE,{"derivedFrom":sQuery(id+"F0.wireOp",EDGE,"E225")}),-1.0]])]});
            var Q4;
            Q4=makeQuery(id+"F0.imprint","IMPRINT",FACE,{"disambiguationData":[TD([[makeQuery(id+"F0.imprint","IMPRINT",EDGE,{"derivedFrom":sQuery(id+"F0.wireOp",EDGE,"E0")}),-1.0]])]});
            var Q5;
            Q5=makeQuery(id+"F0.imprint","IMPRINT",FACE,{"disambiguationData":[TD([[makeQuery(id+"F0.imprint","IMPRINT",EDGE,{"derivedFrom":sQuery(id+"F0.wireOp",EDGE,"E163")}),-1.0]])]});
            extrude(context, id + "F2", {"entities" : qUnion([Q0, Q1, Q2, Q3, Q4, Q5]), "operationType" : NewBodyOperationType.ADD, "depth" : 0.9 * mm, "offsetDistance" : 25 * mm});
        }
        {
            var Q0;
            Q0=makeQuery(id+"F1.opExtrude","CAP_EDGE",EDGE,{"disambiguationData":[OSD([sQuery(id+"F0.wireOp",EDGE,"E236")])],"isStart":true});
            fillet(context, id + "F3", {"entities" : qUnion([Q0]), "radius" : 0.5 * mm, "tangentPropagation" : true, "allowEdgeOverflow" : false});
        }
        {
            var Q0;
            Q0=makeQuery(id+"F1.opExtrude","CAP_FACE",FACE,{"disambiguationData":[OSD([sQuery(id+"F0.wireOp",EDGE,"E236")])],"isStart":false});
            var sketch = newSketch(context, id + "F4", { "sketchPlane" : qUnion([Q0])});
            skCircle(sketch, "E237", {"center": v(0, 0) * mm, "radius": 5.5 * mm});
            skCircle(sketch, "E238", {"center": v(0, 0) * mm, "radius": 4.1 * mm});
            skSolve(sketch);
        }
        {
            var Q0;
            Q0=makeQuery(id+"F4.imprint","IMPRINT",FACE,{"disambiguationData":[TD([[makeQuery(id+"F4.imprint","IMPRINT",EDGE,{"derivedFrom":sQuery(id+"F4.wireOp",EDGE,"E237")}),1.0]])]});
            extrude(context, id + "F5", {"entities" : qUnion([Q0]), "operationType" : NewBodyOperationType.ADD, "depth" : 1 * mm, "offsetDistance" : 25 * mm});
        }
        {
            var Q0;
            Q0=makeQuery(id+"F5.boolean.opBoolean","SPLIT",FACE,{"disambiguationData":[TD([makeQuery(id+"F5.opExtrude","SWEPT_FACE",FACE,{"disambiguationData":[OSD([sQuery(id+"F4.wireOp",EDGE,"E238")])]})])],"derivedFrom":makeQuery(id+"F1.opExtrude","CAP_FACE",FACE,{"disambiguationData":[OSD([sQuery(id+"F0.wireOp",EDGE,"E236")])],"isStart":false})});
            extrude(context, id + "F6", {"entities" : qUnion([Q0]), "operationType" : NewBodyOperationType.ADD, "depth" : 4.5 * mm, "offsetDistance" : 25 * mm});
        }
        {
            var Q0;
            Q0=makeQuery(id+"F6.opExtrude","CAP_EDGE",EDGE,{"disambiguationData":[OSD([sQuery(id+"F4.wireOp",EDGE,"E238")])],"isStart":false});
            fillet(context, id + "F7", {"entities" : qUnion([Q0]), "radius" : 0.5 * mm, "tangentPropagation" : true, "allowEdgeOverflow" : false});
        }
    });
